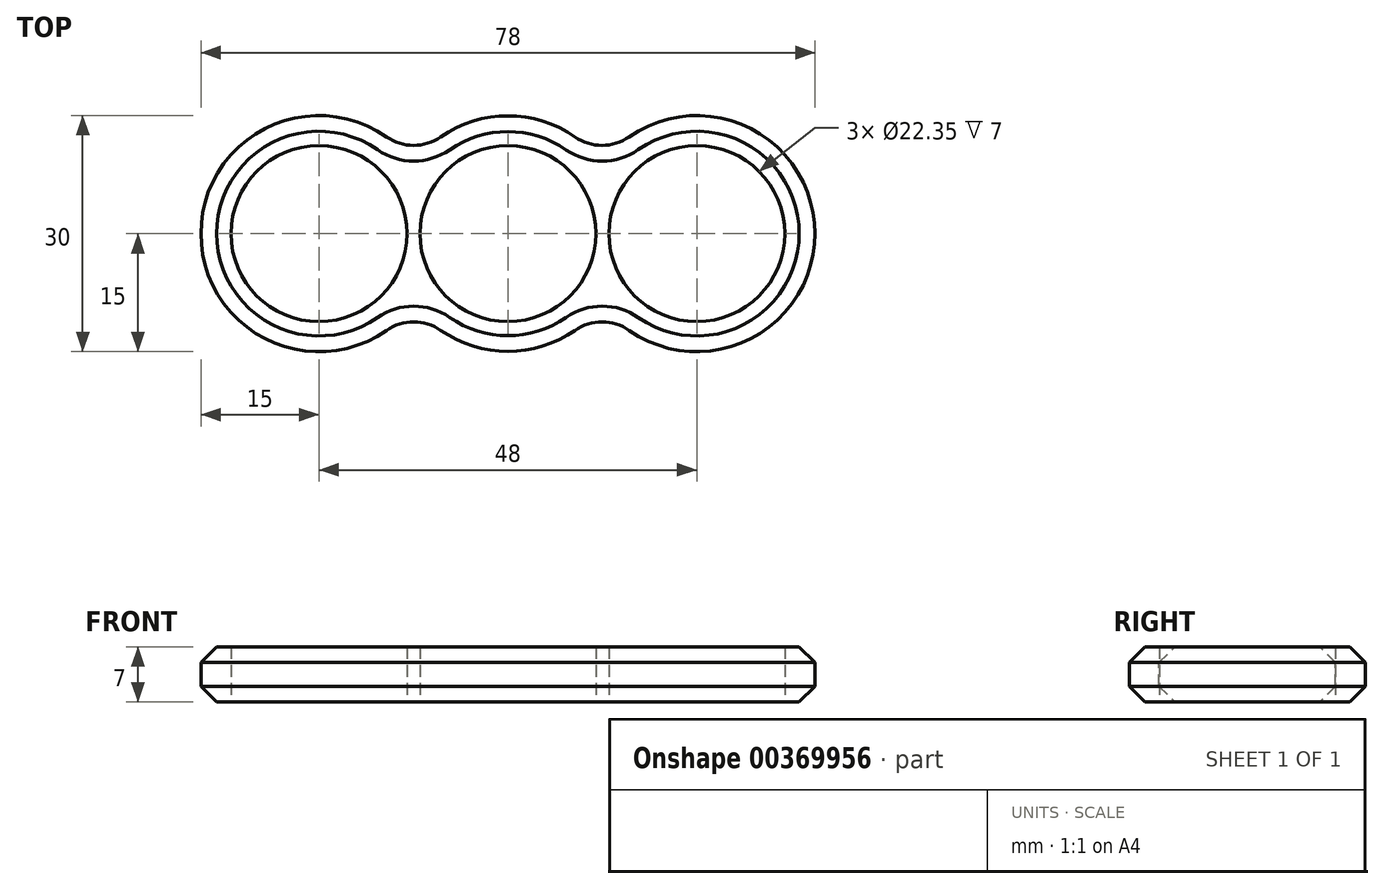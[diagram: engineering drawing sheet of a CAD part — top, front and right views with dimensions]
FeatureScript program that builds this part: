
annotation { "Feature Type Name" : "Feature", "Feature Type Description" : "" }
export const myFeature = defineFeature(function(context is Context, id is Id, definition is map)
    precondition{}
    {
        {
            var Q0;
            Q0=qCreatedBy(makeId("Top.planeOp"),FACE);
            var sketch = newSketch(context, id + "F0", { "sketchPlane" : qUnion([Q0])});
            skCircle(sketch, "E0", {"center": v(0, 0) * mm, "radius": 11.18 * mm});
            skCircle(sketch, "E1", {"center": v(-24, 0) * mm, "radius": 11.18 * mm});
            skCircle(sketch, "E2", {"center": v(24, 0) * mm, "radius": 11.18 * mm});
            skCircle(sketch, "E3", {"center": v(-24, 0) * mm, "radius": 15 * mm});
            skCircle(sketch, "E4", {"center": v(24, 0) * mm, "radius": 15 * mm});
            skCircle(sketch, "E5", {"center": v(0, 0) * mm, "radius": 14.96 * mm});
            skSolve(sketch);
        }
        {
            var Q0;
            Q0=makeQuery(id+"F0.imprint","IMPRINT",FACE,{"disambiguationData":[TD([[makeQuery(id+"F0.imprint","IMPRINT",EDGE,{"derivedFrom":sQuery(id+"F0.wireOp",EDGE,"ffvuShuj-OshO-c5hs-WDAR-ZuKsQZ1vnmAR")}),-1.0]])]});
            var Q1;
            Q1=makeQuery(id+"F0.imprint","IMPRINT",FACE,{"disambiguationData":[TD([[makeQuery(id+"F0.imprint","IMPRINT",EDGE,{"derivedFrom":sQuery(id+"F0.wireOp",EDGE,"bwgdsLH4-RZFz-ohqH-dVLa-YRnHy3qik6SV")}),-1.0]])]});
            var Q2;
            Q2=makeQuery(id+"F0.imprint","IMPRINT",FACE,{"disambiguationData":[TD([[makeQuery(id+"F0.imprint","IMPRINT",EDGE,{"derivedFrom":sQuery(id+"F0.wireOp",EDGE,"TINXS8bJ-a08q-0g3v-jvgb-TxoOEa6wy1WR")}),-1.0]])]});
            var Q3;
            {var subQ0=sQuery(id+"F0.wireOp",EDGE,"9GnjF5dk-10nB-Mq5b-Iskw-ds0yqw7a4ucy");var subQ1=sQuery(id+"F0.wireOp",EDGE,"FzkzEjta-EPXN-Z5uv-5ILG-J4rEEolZ74wE");var subQ2=makeQuery(id+"F0.imprint","INTERSECT",VERTEX,{"disambiguationData":[OD(1.0)],"derivedFrom":[subQ1,subQ0]});Q3=makeQuery(id+"F0.imprint","IMPRINT",FACE,{"disambiguationData":[TD([[makeQuery(id+"F0.imprint","IMPRINT",EDGE,{"disambiguationData":[TD([[subQ2,-1.0]])],"derivedFrom":subQ1}),-1.0]])]});}
            var Q4;
            {var subQ0=sQuery(id+"F0.wireOp",EDGE,"6ec109ea-0f7a-418d-82a9-b200b767a9cb0.MirrorCS");var subQ1=sQuery(id+"F0.wireOp",EDGE,"FzkzEjta-EPXN-Z5uv-5ILG-J4rEEolZ74wE");var subQ2=makeQuery(id+"F0.imprint","INTERSECT",VERTEX,{"disambiguationData":[OD(1.0)],"derivedFrom":[subQ1,subQ0]});Q4=makeQuery(id+"F0.imprint","IMPRINT",FACE,{"disambiguationData":[TD([[makeQuery(id+"F0.imprint","IMPRINT",EDGE,{"disambiguationData":[TD([[subQ2,1.0]])],"derivedFrom":subQ1}),-1.0]])]});}
            var Q5;
            {var subQ0=sQuery(id+"F0.wireOp",EDGE,"99vP87gl-wvMF-NPdc-mqaH-cfolrdlP8JtZ");var subQ1=sQuery(id+"F0.wireOp",EDGE,"FzkzEjta-EPXN-Z5uv-5ILG-J4rEEolZ74wE");var subQ2=makeQuery(id+"F0.imprint","INTERSECT",VERTEX,{"disambiguationData":[OD(1.0)],"derivedFrom":[subQ1,subQ0]});Q5=makeQuery(id+"F0.imprint","IMPRINT",FACE,{"disambiguationData":[TD([[makeQuery(id+"F0.imprint","IMPRINT",EDGE,{"disambiguationData":[TD([[subQ2,1.0]])],"derivedFrom":subQ1}),-1.0]])]});}
            var Q6;
            {var subQ0=sQuery(id+"F0.wireOp",EDGE,"FzkzEjta-EPXN-Z5uv-5ILG-J4rEEolZ74wE");var subQ1=makeQuery(id+"F0.imprint","INTERSECT",VERTEX,{"derivedFrom":[sQuery(id+"F0.wireOp",EDGE,"b2ixpRwv-Uinv-SrGr-89pi-S0W5oyQQp6Q2"),subQ0]});Q6=makeQuery(id+"F0.imprint","IMPRINT",FACE,{"disambiguationData":[TD([[makeQuery(id+"F0.imprint","IMPRINT",EDGE,{"disambiguationData":[TD([[subQ1,1.0]])],"derivedFrom":subQ0}),-1.0]])]});}
            var Q7;
            {var subQ0=sQuery(id+"F0.wireOp",EDGE,"E5");var subQ1=sQuery(id+"F0.wireOp",EDGE,"E1");var subQ2=makeQuery(id+"F0.imprint","INTERSECT",VERTEX,{"disambiguationData":[OD(0.0)],"derivedFrom":[subQ1,subQ0]});Q7=makeQuery(id+"F0.imprint","IMPRINT",FACE,{"disambiguationData":[TD([[makeQuery(id+"F0.imprint","IMPRINT",EDGE,{"disambiguationData":[TD([[subQ2,-1.0]])],"derivedFrom":subQ1}),-1.0]])]});}
            var Q8;
            {var subQ1=sQuery(id+"F0.wireOp",EDGE,"E3");var subQ3=sQuery(id+"F0.wireOp",EDGE,"E0");var subQ4=makeQuery(id+"F0.imprint","INTERSECT",VERTEX,{"disambiguationData":[OD(0.0)],"derivedFrom":[subQ3,subQ1]});Q8=makeQuery(id+"F0.imprint","IMPRINT",FACE,{"disambiguationData":[TD([[makeQuery(id+"F0.imprint","IMPRINT",EDGE,{"disambiguationData":[TD([[subQ4,-1.0]])],"derivedFrom":subQ3}),-1.0]])]});}
            var Q9;
            {var subQ0=sQuery(id+"F0.wireOp",EDGE,"E3");var subQ1=sQuery(id+"F0.wireOp",EDGE,"E0");var subQ2=makeQuery(id+"F0.imprint","INTERSECT",VERTEX,{"disambiguationData":[OD(0.0)],"derivedFrom":[subQ1,subQ0]});Q9=makeQuery(id+"F0.imprint","IMPRINT",FACE,{"disambiguationData":[TD([[makeQuery(id+"F0.imprint","IMPRINT",EDGE,{"disambiguationData":[TD([[subQ2,1.0]])],"derivedFrom":subQ1}),-1.0]])]});}
            var Q10;
            {var subQ1=sQuery(id+"F0.wireOp",EDGE,"E4");var subQ3=sQuery(id+"F0.wireOp",EDGE,"E0");var subQ5=makeQuery(id+"F0.imprint","INTERSECT",VERTEX,{"disambiguationData":[OD(0.0)],"derivedFrom":[subQ3,subQ1]});Q10=makeQuery(id+"F0.imprint","IMPRINT",FACE,{"disambiguationData":[TD([[makeQuery(id+"F0.imprint","IMPRINT",EDGE,{"disambiguationData":[TD([[subQ5,1.0]])],"derivedFrom":subQ3}),-1.0]])]});}
            var Q11;
            {var subQ0=sQuery(id+"F0.wireOp",EDGE,"E5");var subQ1=sQuery(id+"F0.wireOp",EDGE,"E2");var subQ2=makeQuery(id+"F0.imprint","INTERSECT",VERTEX,{"disambiguationData":[OD(0.0)],"derivedFrom":[subQ1,subQ0]});Q11=makeQuery(id+"F0.imprint","IMPRINT",FACE,{"disambiguationData":[TD([[makeQuery(id+"F0.imprint","IMPRINT",EDGE,{"disambiguationData":[TD([[subQ2,1.0]])],"derivedFrom":subQ1}),-1.0]])]});}
            var Q12;
            {var subQ0=sQuery(id+"F0.wireOp",EDGE,"E3");var subQ1=sQuery(id+"F0.wireOp",EDGE,"E0");var subQ2=makeQuery(id+"F0.imprint","INTERSECT",VERTEX,{"disambiguationData":[OD(1.0)],"derivedFrom":[subQ1,subQ0]});Q12=makeQuery(id+"F0.imprint","IMPRINT",FACE,{"disambiguationData":[TD([[makeQuery(id+"F0.imprint","IMPRINT",EDGE,{"disambiguationData":[TD([[subQ2,-1.0]])],"derivedFrom":subQ1}),-1.0]])]});}
            var Q13;
            Q13=makeQuery(id+"F0.imprint","IMPRINT",FACE,{"disambiguationData":[TD([[makeQuery(id+"F0.imprint","IMPRINT",EDGE,{"derivedFrom":sQuery(id+"F0.wireOp",EDGE,"E2")}),-1.0]])]});
            var Q14;
            Q14=makeQuery(id+"F0.imprint","IMPRINT",FACE,{"disambiguationData":[TD([[makeQuery(id+"F0.imprint","IMPRINT",EDGE,{"derivedFrom":sQuery(id+"F0.wireOp",EDGE,"E1")}),-1.0]])]});
            extrude(context, id + "F1", {"entities" : qUnion([Q0, Q1, Q2, Q3, Q4, Q5, Q6, Q7, Q8, Q9, Q10, Q11, Q12, Q13, Q14]), "depth" : 7 * mm, "offsetDistance" : 25 * mm});
        }
        {
            var Q0;
            {var subQ0=sQuery(id+"F0.wireOp",EDGE,"E5");var subQ1=sQuery(id+"F0.wireOp",EDGE,"E3");Q0=makeQuery(id+"F1.opExtrude","SWEPT_EDGE",EDGE,{"disambiguationData":[OSD([subQ1,subQ0]),TDD([makeQuery(id+"F0.imprint","INTERSECT",VERTEX,{"disambiguationData":[OD(1.0)],"derivedFrom":[subQ1,subQ0]})])]});}
            var Q1;
            {var subQ0=sQuery(id+"F0.wireOp",EDGE,"E5");var subQ1=sQuery(id+"F0.wireOp",EDGE,"E4");Q1=makeQuery(id+"F1.opExtrude","SWEPT_EDGE",EDGE,{"disambiguationData":[OSD([subQ1,subQ0]),TDD([makeQuery(id+"F0.imprint","INTERSECT",VERTEX,{"disambiguationData":[OD(1.0)],"derivedFrom":[subQ1,subQ0]})])]});}
            var Q2;
            {var subQ0=sQuery(id+"F0.wireOp",EDGE,"E5");var subQ1=sQuery(id+"F0.wireOp",EDGE,"E4");Q2=makeQuery(id+"F1.opExtrude","SWEPT_EDGE",EDGE,{"disambiguationData":[OSD([subQ1,subQ0]),TDD([makeQuery(id+"F0.imprint","INTERSECT",VERTEX,{"disambiguationData":[OD(0.0)],"derivedFrom":[subQ1,subQ0]})])]});}
            var Q3;
            {var subQ0=sQuery(id+"F0.wireOp",EDGE,"E5");var subQ1=sQuery(id+"F0.wireOp",EDGE,"E3");Q3=makeQuery(id+"F1.opExtrude","SWEPT_EDGE",EDGE,{"disambiguationData":[OSD([subQ1,subQ0]),TDD([makeQuery(id+"F0.imprint","INTERSECT",VERTEX,{"disambiguationData":[OD(0.0)],"derivedFrom":[subQ1,subQ0]})])]});}
            fillet(context, id + "F2", {"entities" : qUnion([Q0, Q1, Q2, Q3]), "radius" : 6 * mm, "tangentPropagation" : true, "allowEdgeOverflow" : false});
        }
        {
            var Q0;
            Q0=makeQuery(id+"F1.opExtrude","CAP_EDGE",EDGE,{"disambiguationData":[OSD([sQuery(id+"F0.wireOp",EDGE,"E3")])],"isStart":true});
            var Q1;
            Q1=makeQuery(id+"F1.opExtrude","CAP_EDGE",EDGE,{"disambiguationData":[OSD([sQuery(id+"F0.wireOp",EDGE,"E3")])],"isStart":false});
            chamfer(context, id + "F3", {"entities" : qUnion([Q0, Q1]), "width" : 2 * mm, "tangentPropagation" : true});
        }
    });
